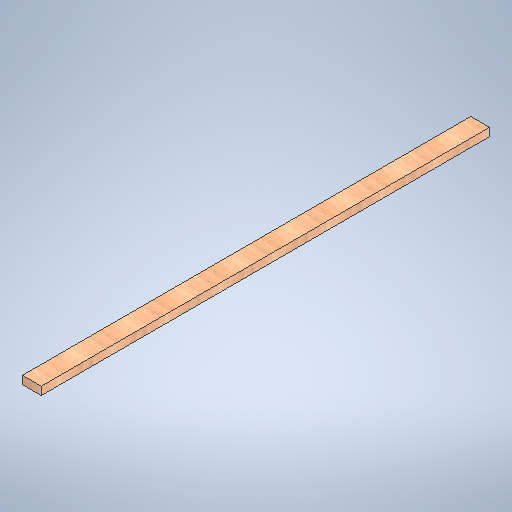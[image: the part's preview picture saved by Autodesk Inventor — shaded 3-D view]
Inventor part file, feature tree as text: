
AUTODESK INVENTOR PART (.ipt)
format: ipt  version: 2025.1 (Build 291241020, 241B)  size: 284,672 bytes
history: native  units: in
note: dims shown in document units (in); Inventor stores cm internally (conversion verified against a paired STEP export)
features: extrude x1, sketch x1
ambient origin geometry x8: Origin, YZ Plane, XZ Plane, XY Plane, X Axis, Y Axis, Z Axis, Center Point
bodies: Solid1 (feature_tree)
feature tree (2):
  extrude  "Extrusion1"  Depth=1.5in TaperAngle=0.0deg
  sketch  "Sketch1"  dims[d1=3.5in d2=1.5in d3=0.0in d4=83.35in]
